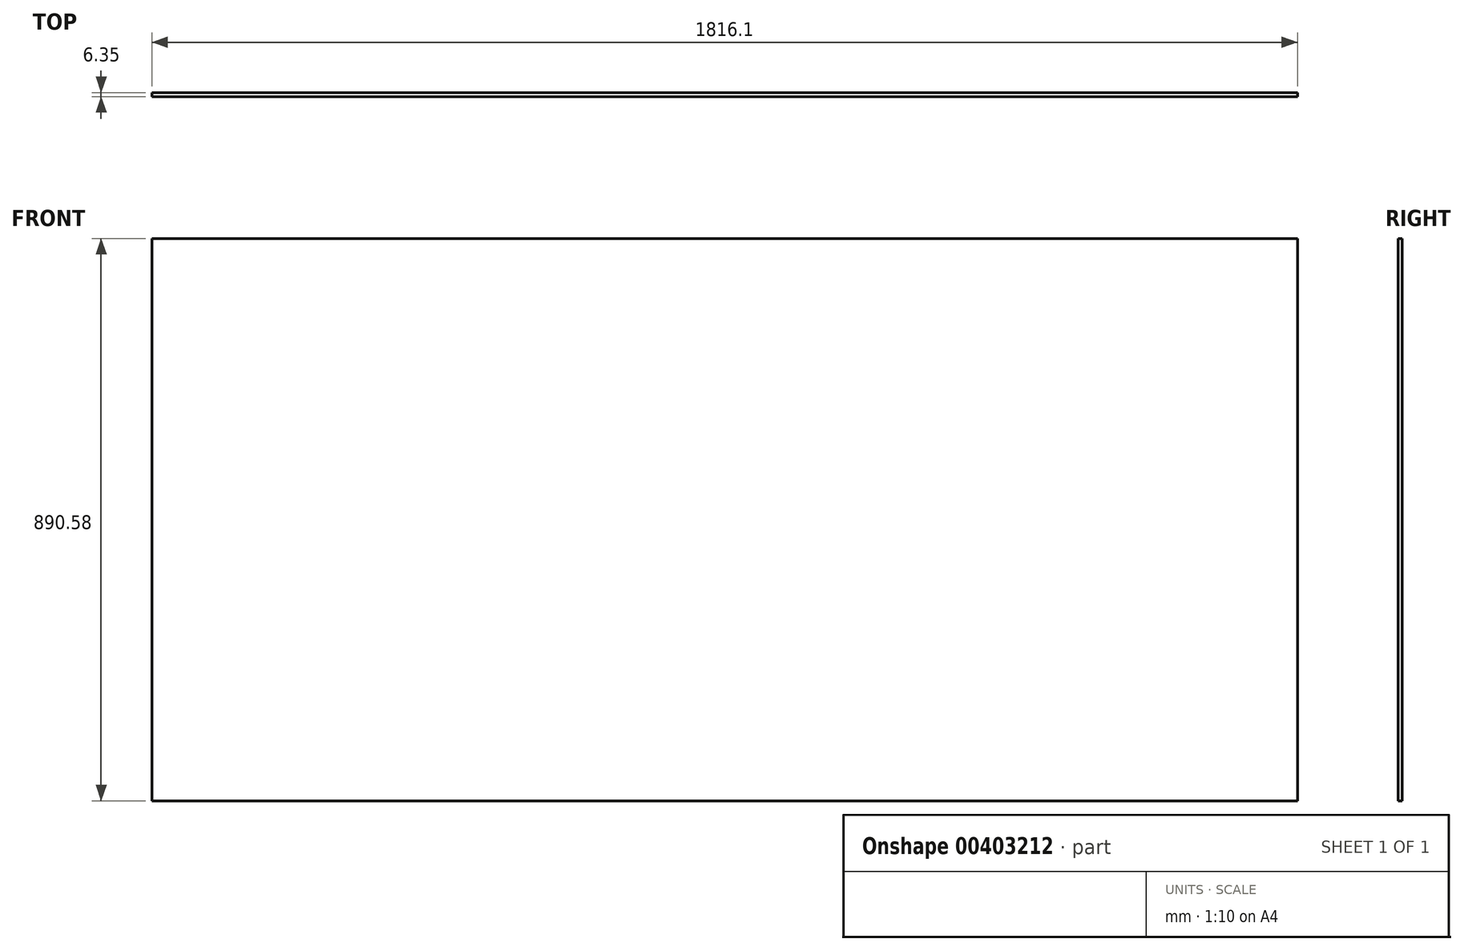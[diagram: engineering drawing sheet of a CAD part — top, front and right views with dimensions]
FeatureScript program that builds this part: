
annotation { "Feature Type Name" : "Feature", "Feature Type Description" : "" }
export const myFeature = defineFeature(function(context is Context, id is Id, definition is map)
    precondition{}
    {
        {
            var Q0;
            Q0=qCreatedBy(makeId("Front.planeOp"),FACE);
            var sketch = newSketch(context, id + "F0", { "sketchPlane" : qUnion([Q0])});
            skLineSegment(sketch, "E0.bottom", {"start": v(908.05, 445.3) * mm, "end": v(-908.05, 445.3) * mm});
            skLineSegment(sketch, "E0.top", {"start": v(908.05, -445.3) * mm, "end": v(-908.05, -445.3) * mm});
            skLineSegment(sketch, "E0.left", {"start": v(908.05, 445.3) * mm, "end": v(908.05, -445.3) * mm});
            skLineSegment(sketch, "E0.right", {"start": v(-908.05, 445.3) * mm, "end": v(-908.05, -445.3) * mm});
            skPoint(sketch, "E0.middle", {"position": v(0, 0) * mm});
            skSolve(sketch);
        }
        {
            var Q0;
            Q0=qSketchRegion(id+"F0",true);
            extrude(context, id + "F1", {"entities" : qUnion([Q0]), "depth" : 6.35 * mm});
        }
    });
